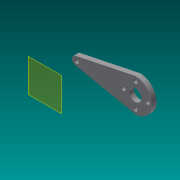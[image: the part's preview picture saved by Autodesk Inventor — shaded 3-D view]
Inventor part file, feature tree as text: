
AUTODESK INVENTOR PART (.ipt)
format: ipt  version: 2013 SP2 (Build 170200200, 200)  size: 104,448 bytes
history: native  units: in
note: dims shown in document units (in); Inventor stores cm internally (conversion verified against a paired STEP export)
features: sheet_metal_op x1, sketch x1, other x1, plane x1
ambient origin geometry x8: Origin, YZ Plane, XZ Plane, XY Plane, X Axis, Y Axis, Z Axis, Center Point
bodies: Solid1 (feature_tree)
feature tree (4):
  sheet_metal_op  "Face1"
  sketch  "Sketch1"  dims[d1=0.118in d2=0.125in]
  other  "Plate1"
  plane  "Work Plane2"
